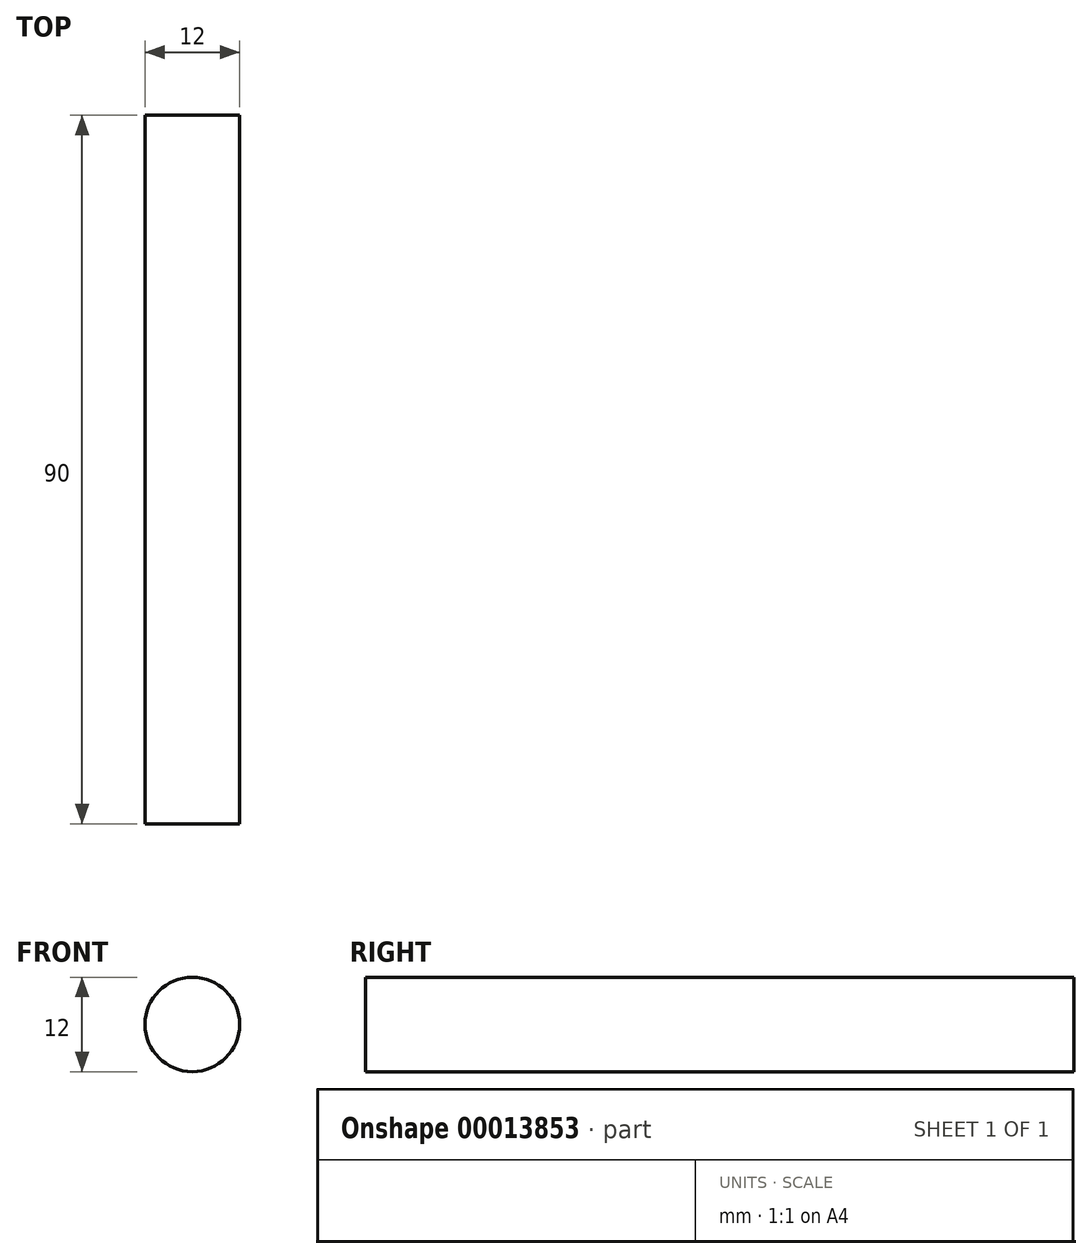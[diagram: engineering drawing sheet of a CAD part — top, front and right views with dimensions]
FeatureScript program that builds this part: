
annotation { "Feature Type Name" : "Feature", "Feature Type Description" : "" }
export const myFeature = defineFeature(function(context is Context, id is Id, definition is map)
    precondition{}
    {
        {
            var Q0;
            Q0=qCreatedBy(makeId("Right.planeOp"),FACE);
            var sketch = newSketch(context, id + "F0", { "sketchPlane" : qUnion([Q0])});
            skLineSegment(sketch, "E0.bottom", {"start": v(-45, 0) * mm, "end": v(45, 0) * mm});
            skLineSegment(sketch, "E0.top", {"start": v(-45, 6) * mm, "end": v(45, 6) * mm});
            skLineSegment(sketch, "E0.left", {"start": v(-45, 0) * mm, "end": v(-45, 6) * mm});
            skLineSegment(sketch, "E0.right", {"start": v(45, 0) * mm, "end": v(45, 6) * mm});
            skSolve(sketch);
        }
        {
            var Q0;
            Q0 = qSketchRegion(id + "F0", true);
            var Q1;
            Q1=sQuery(id+"F0.wireOp",EDGE,"E0.bottom");
            revolve(context, id + "F1", {"entities" : qUnion([Q0]), "axis" : qUnion([Q1]), "revolveType" : RevolveType.FULL});
        }
    });
